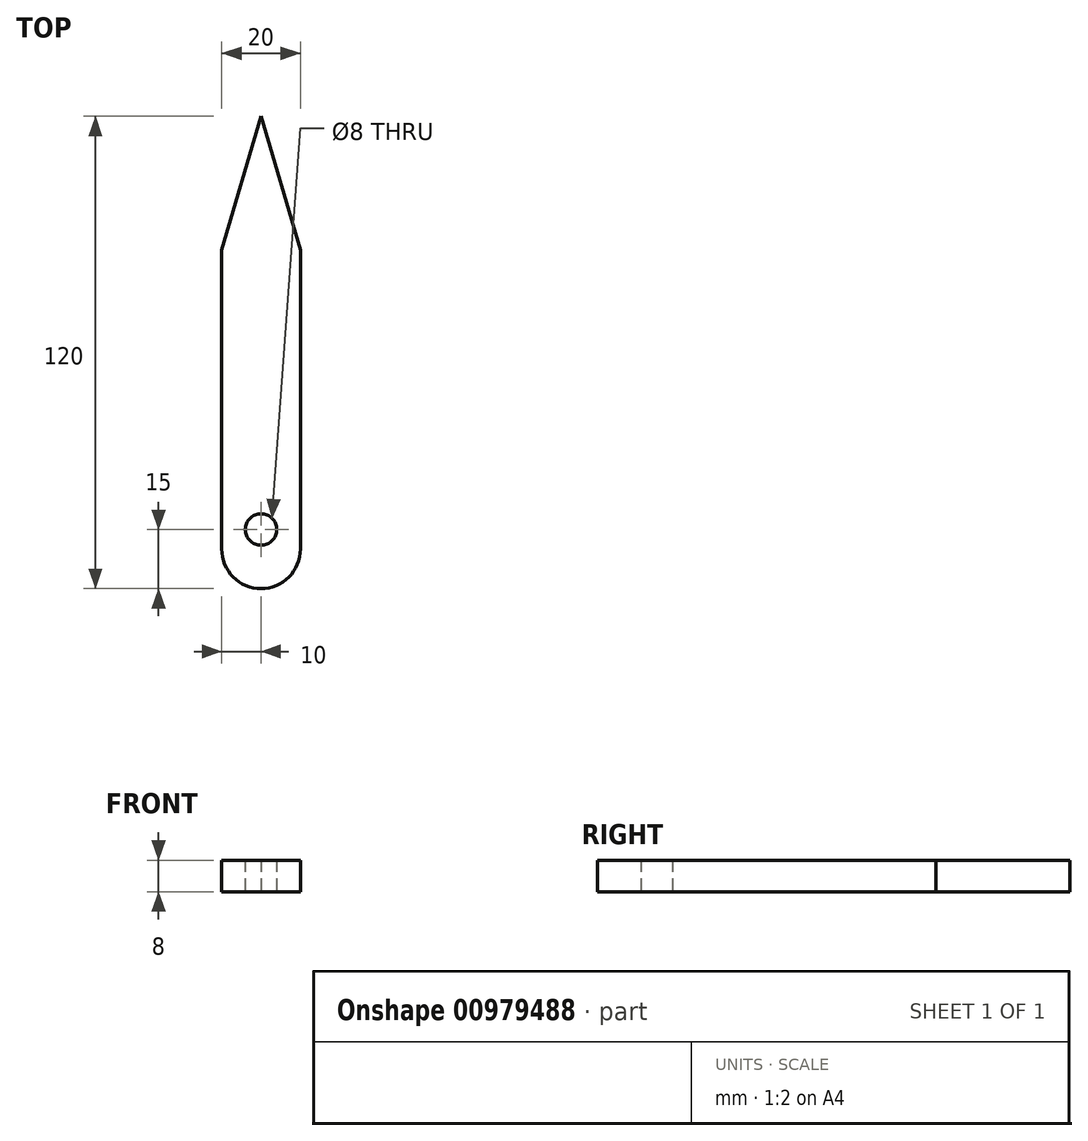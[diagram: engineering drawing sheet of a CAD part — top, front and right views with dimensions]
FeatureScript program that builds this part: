
annotation { "Feature Type Name" : "Feature", "Feature Type Description" : "" }
export const myFeature = defineFeature(function(context is Context, id is Id, definition is map)
    precondition{}
    {
        {
            var Q0;
            Q0=qCreatedBy(makeId("Top.planeOp"),FACE);
            var sketch = newSketch(context, id + "F0", { "sketchPlane" : qUnion([Q0])});
            skLineSegment(sketch, "E0.bottom", {"start": v(10, 0) * mm, "end": v(10, 0) * mm});
            skCircle(sketch, "E1", {"center": v(10, 15) * mm, "radius": 4 * mm});
            skPoint(sketch, "E2.visualSharp", {"position": v(0, 0) * mm});
            skArc(sketch, "E2.filletArc", {"start": v(0, 10) * mm, "mid": v(2.93, 2.93) * mm, "end": v(10, 0) * mm});
            skPoint(sketch, "E3.visualSharp", {"position": v(20, 0) * mm});
            skArc(sketch, "E3.filletArc", {"start": v(10, 0) * mm, "mid": v(17.07, 2.93) * mm, "end": v(20, 10) * mm});
            skLineSegment(sketch, "E4", {"start": v(10, 120) * mm, "end": v(0, 85.95) * mm});
            skLineSegment(sketch, "E5", {"start": v(10, 120) * mm, "end": v(20, 85.95) * mm});
            skLineSegment(sketch, "E6", {"start": v(0, 85.95) * mm, "end": v(0, 10) * mm});
            skLineSegment(sketch, "E7", {"start": v(20, 85.95) * mm, "end": v(20, 10) * mm});
            skSolve(sketch);
        }
        {
            var Q0;
            Q0=makeQuery(id+"F0.imprint","IMPRINT",FACE,{"disambiguationData":[TD([[makeQuery(id+"F0.imprint","IMPRINT",EDGE,{"derivedFrom":sQuery(id+"F0.wireOp",EDGE,"E1")}),-1.0]])]});
            extrude(context, id + "F1", {"entities" : qUnion([Q0]), "depth" : 8 * mm, "offsetDistance" : 25 * mm});
        }
    });
